# Revit family: Plumbing-Faucet-Sloan-Valve-EDF-100x
name_source: partatom
category: Plumbing Fixtures
units: mm (PartAtom-declared; Revit-internal decimal feet)

## family parameters
Cut with Voids When Loaded = No
Host = Face
Maintain Annotation Orientation = No
OmniClass Number = 23.45.55.14
OmniClass Title = Single Faucets
Part Type = Normal
Room Calculation Point = No
Round Connector Dimension = Use Diameter
Shared = No

## types (1)
- Not a Type - Load Type Catalog!
    Apparent Load = 0 VA
    Assembly Code = D2010
    Battery Powered = No
    CW Connection = Yes
    CWFU = 1.5
    Cold Water Connection Diameter = 1"
    Current = 0 A
    Default Elevation = 0"
    Depth = 6 1/2"
    Description = Touch-free, electronically controlled washbasin faucet with temperature-mixing: sturdy metal housing, chromed; infrared sensors with automatic setting feature, microprocessor; reliable solenoid valve and spray head; hot and cold water supply connection with flexible high-pressure hoses; check valves and filters (built in); temperature freely selectable or preselectable (vandal-proof cover); hot limit stop adjustable; temporary off (cleaning) and continuous on (filling) activatable via IR-Touch field; continuous on and hygiene rinse time adjustable via IR-Touch field; water follow-up time and sensor sensitivity adjustable via IR-Touch field; 12, 24 or 48 hours hygienic rinse can be activated via IR-Touch field; installation like conventional single-lever faucet.
Prepared for mains: alternative power supplies (see accessories),transformer box.
    Edition number = 1
    HW Connection = Yes
    HWFU = 1.5
    Hardwired = Yes
    Height = 6"
    Hot Water Connection Diameter = 1"
    Hot/Cold Water Supply = Yes
    Keynote = 15410
    Manufacturer = Sloan Valve
    Model = Model not specified - Load type catalog
    Number of Poles = 1
    Power Factor = 1
    Product Material = Sloan Valve - Finish - Polished Chrome
    URL = www.sloanvalve.com
    Valve Pressure Drop = 0.00 psi
    Vent Connection = No
    Version = 1
    Voltage = 24 V
    WFU = 0
    Waste Connection = No
    Water Flow = 2 GPM
    Width = 2 1/2"
    z_Connector Position = 1/2"

## geometry (parser evidence)
native form markers: Sweep x8
no freeform markers — native parametric forms only
